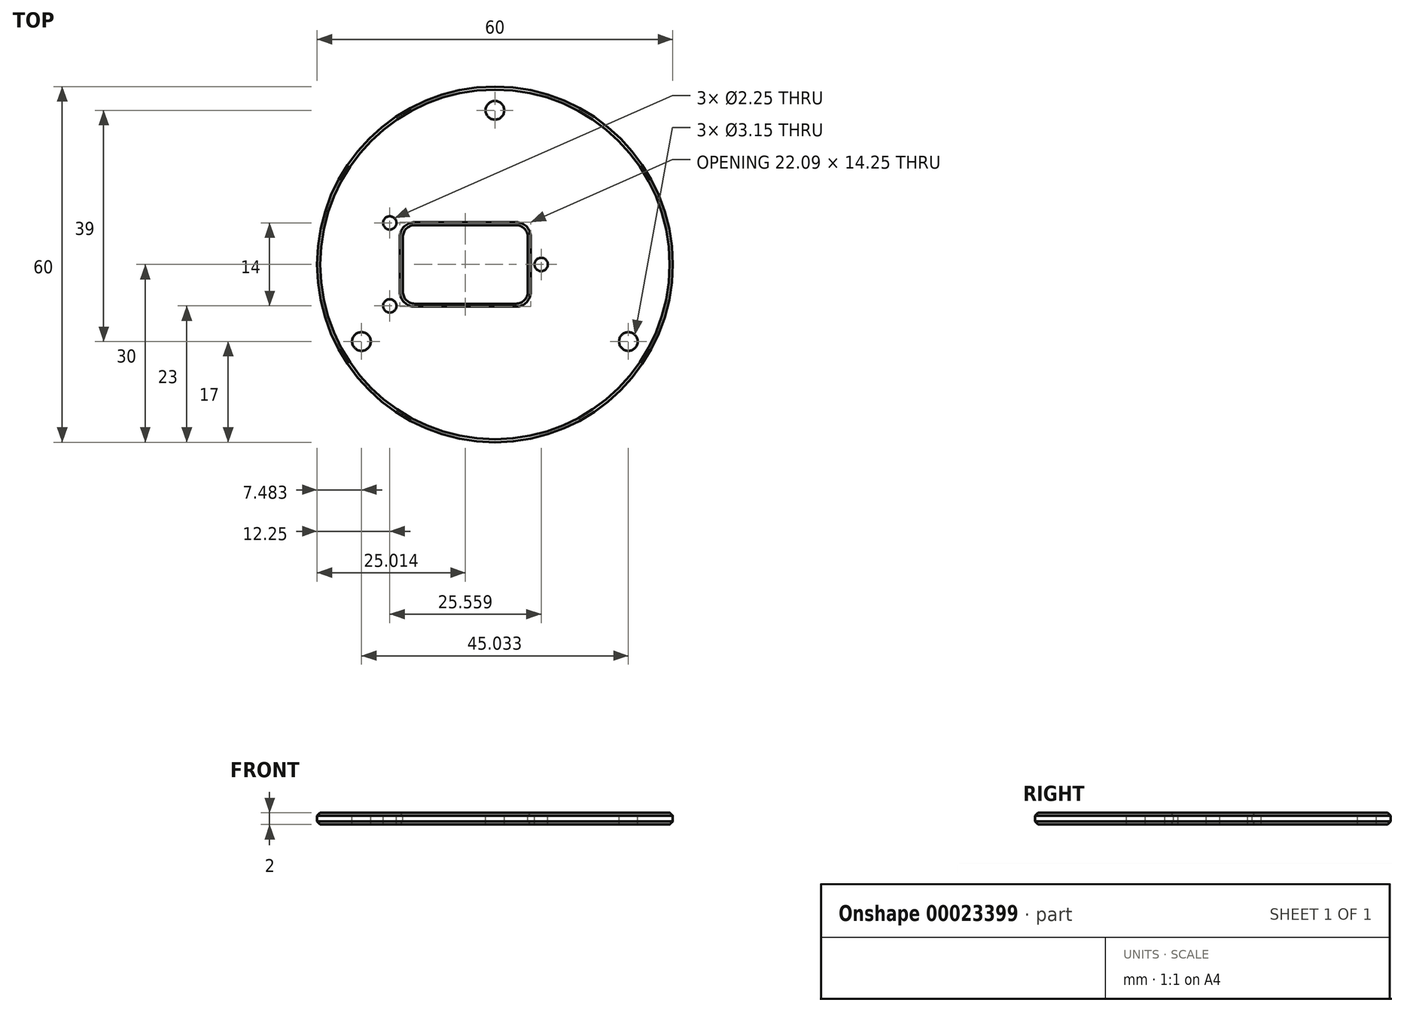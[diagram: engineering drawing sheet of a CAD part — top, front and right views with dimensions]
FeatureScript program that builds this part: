
annotation { "Feature Type Name" : "Feature", "Feature Type Description" : "" }
export const myFeature = defineFeature(function(context is Context, id is Id, definition is map)
    precondition{}
    {
        {
            var Q0;
            Q0=qCreatedBy(makeId("Top.planeOp"),FACE);
            var sketch = newSketch(context, id + "F0", { "sketchPlane" : qUnion([Q0])});
            skCircle(sketch, "E0", {"center": v(0, 0) * mm, "radius": 35 * mm, "construction": true});
            skCircle(sketch, "E1", {"center": v(0, 0) * mm, "radius": 30 * mm});
            skLineSegment(sketch, "E2.bottom", {"start": v(-18.75, 8.88) * mm, "end": v(18.75, 8.88) * mm, "construction": true});
            skLineSegment(sketch, "E2.top", {"start": v(-18.75, -8.87) * mm, "end": v(18.75, -8.88) * mm, "construction": true});
            skLineSegment(sketch, "E2.left", {"start": v(-18.75, 8.87) * mm, "end": v(-18.75, -8.88) * mm, "construction": true});
            skLineSegment(sketch, "E2.right", {"start": v(18.75, 8.87) * mm, "end": v(18.75, -8.88) * mm, "construction": true});
            skLineSegment(sketch, "E3", {"start": v(-17.75, 7) * mm, "end": v(-17.75, -7) * mm, "construction": true});
            skCircle(sketch, "E4", {"center": v(-17.75, 7) * mm, "radius": 1.13 * mm});
            skCircle(sketch, "E5", {"center": v(-17.75, -7) * mm, "radius": 1.13 * mm});
            skCircle(sketch, "E6", {"center": v(7.8, 0) * mm, "radius": 1.13 * mm});
            skLineSegment(sketch, "E7", {"start": v(-17.75, 7) * mm, "end": v(7.8, 0) * mm, "construction": true});
            skLineSegment(sketch, "E8", {"start": v(7.8, 0) * mm, "end": v(-17.75, -7) * mm, "construction": true});
            skLineSegment(sketch, "E9", {"start": v(-17.75, -7) * mm, "end": v(-17.75, -8.87) * mm, "construction": true});
            skLineSegment(sketch, "E10", {"start": v(-17.75, 8.88) * mm, "end": v(-17.75, 7) * mm, "construction": true});
            skLineSegment(sketch, "E11", {"start": v(-17.75, 7) * mm, "end": v(-18.75, 7) * mm, "construction": true});
            skPoint(sketch, "E12", {"position": v(0, 8.88) * mm});
            skPoint(sketch, "E13", {"position": v(18.75, 0) * mm});
            skCircle(sketch, "E14.cCircle", {"center": v(0, 0) * mm, "radius": 26 * mm, "construction": true});
            skLineSegment(sketch, "E14.0", {"start": v(0, 26) * mm, "end": v(22.52, -13) * mm, "construction": true});
            skLineSegment(sketch, "E14.1", {"start": v(22.52, -13) * mm, "end": v(-22.52, -13) * mm, "construction": true});
            skLineSegment(sketch, "E14.2", {"start": v(-22.52, -13) * mm, "end": v(0, 26) * mm, "construction": true});
            skCircle(sketch, "E15", {"center": v(0, 26) * mm, "radius": 1.57 * mm});
            skCircle(sketch, "E16", {"center": v(22.52, -13) * mm, "radius": 1.57 * mm});
            skCircle(sketch, "E17", {"center": v(-22.52, -13) * mm, "radius": 1.57 * mm});
            skLineSegment(sketch, "E18.bottom", {"start": v(-15.53, 6.63) * mm, "end": v(5.56, 6.63) * mm});
            skLineSegment(sketch, "E18.top", {"start": v(-15.53, -6.62) * mm, "end": v(5.56, -6.62) * mm});
            skLineSegment(sketch, "E18.left", {"start": v(-15.53, 6.63) * mm, "end": v(-15.53, -6.62) * mm});
            skLineSegment(sketch, "E18.right", {"start": v(5.56, 6.63) * mm, "end": v(5.56, -6.62) * mm});
            skSolve(sketch);
        }
        {
            var Q0;
            Q0=makeQuery(id+"F0.imprint","IMPRINT",FACE,{"disambiguationData":[TD([[makeQuery(id+"F0.imprint","IMPRINT",EDGE,{"derivedFrom":sQuery(id+"F0.wireOp",EDGE,"E1")}),1.0]])]});
            extrude(context, id + "F1", {"entities" : qUnion([Q0]), "oppositeDirection" : true, "depth" : 2 * mm});
        }
        {
            var Q0;
            Q0=makeQuery(id+"F1.opExtrude","SWEPT_EDGE",EDGE,{"disambiguationData":[OSD([sQuery(id+"F0.wireOp",EDGE,"E18.bottom"),sQuery(id+"F0.wireOp",EDGE,"E18.left")])]});
            var Q1;
            Q1=makeQuery(id+"F1.opExtrude","SWEPT_EDGE",EDGE,{"disambiguationData":[OSD([sQuery(id+"F0.wireOp",EDGE,"E18.top"),sQuery(id+"F0.wireOp",EDGE,"E18.left")])]});
            var Q2;
            Q2=makeQuery(id+"F1.opExtrude","SWEPT_EDGE",EDGE,{"disambiguationData":[OSD([sQuery(id+"F0.wireOp",EDGE,"E18.top"),sQuery(id+"F0.wireOp",EDGE,"E18.right")])]});
            var Q3;
            Q3=makeQuery(id+"F1.opExtrude","SWEPT_EDGE",EDGE,{"disambiguationData":[OSD([sQuery(id+"F0.wireOp",EDGE,"E18.bottom"),sQuery(id+"F0.wireOp",EDGE,"E18.right")])]});
            fillet(context, id + "F2", {"entities" : qUnion([Q0, Q1, Q2, Q3]), "radius" : 2 * mm, "tangentPropagation" : true, "allowEdgeOverflow" : false});
        }
        {
            var Q0;
            Q0=makeQuery(id+"F1.opExtrude","CAP_EDGE",EDGE,{"disambiguationData":[OSD([sQuery(id+"F0.wireOp",EDGE,"E18.bottom")])],"isStart":false});
            var Q1;
            Q1=makeQuery(id+"F1.opExtrude","CAP_EDGE",EDGE,{"disambiguationData":[OSD([sQuery(id+"F0.wireOp",EDGE,"E18.bottom")])],"isStart":true});
            var Q2;
            Q2=makeQuery(id+"F1.opExtrude","CAP_EDGE",EDGE,{"disambiguationData":[OSD([sQuery(id+"F0.wireOp",EDGE,"E1")])],"isStart":true});
            var Q3;
            Q3=makeQuery(id+"F1.opExtrude","CAP_EDGE",EDGE,{"disambiguationData":[OSD([sQuery(id+"F0.wireOp",EDGE,"E1")])],"isStart":false});
            chamfer(context, id + "F3", {"entities" : qUnion([Q0, Q1, Q2, Q3]), "width" : .5 * mm, "tangentPropagation" : true});
        }
    });
